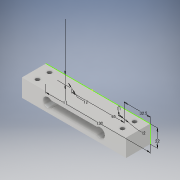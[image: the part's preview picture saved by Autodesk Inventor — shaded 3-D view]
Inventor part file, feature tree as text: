
AUTODESK INVENTOR PART (.ipt)
format: ipt  version: 2019 (Build 230136000, 136)  size: 137,216 bytes
history: native  units: mm
features: sketch x2, extrude x2, other x1, hole x1
ambient origin geometry x8: Origin, YZ Plane, XZ Plane, XY Plane, X Axis, Y Axis, Z Axis, Center Point
bodies: Body1 (feature_tree)
feature tree (6):
  other  "ソリッド1"
  sketch  "スケッチ1"
  extrude  "押し出し1"  Depth=130.0mm
  extrude  "押し出し2"  Depth=22.0mm
  hole  "穴1"  [1 undecoded]
  sketch  "スケッチ2"
note: 1 required parameter value undecoded (feature->parameter linkage not recoverable at this tier; creation-order binding heuristic only, values carry confidence <= 0.55)
